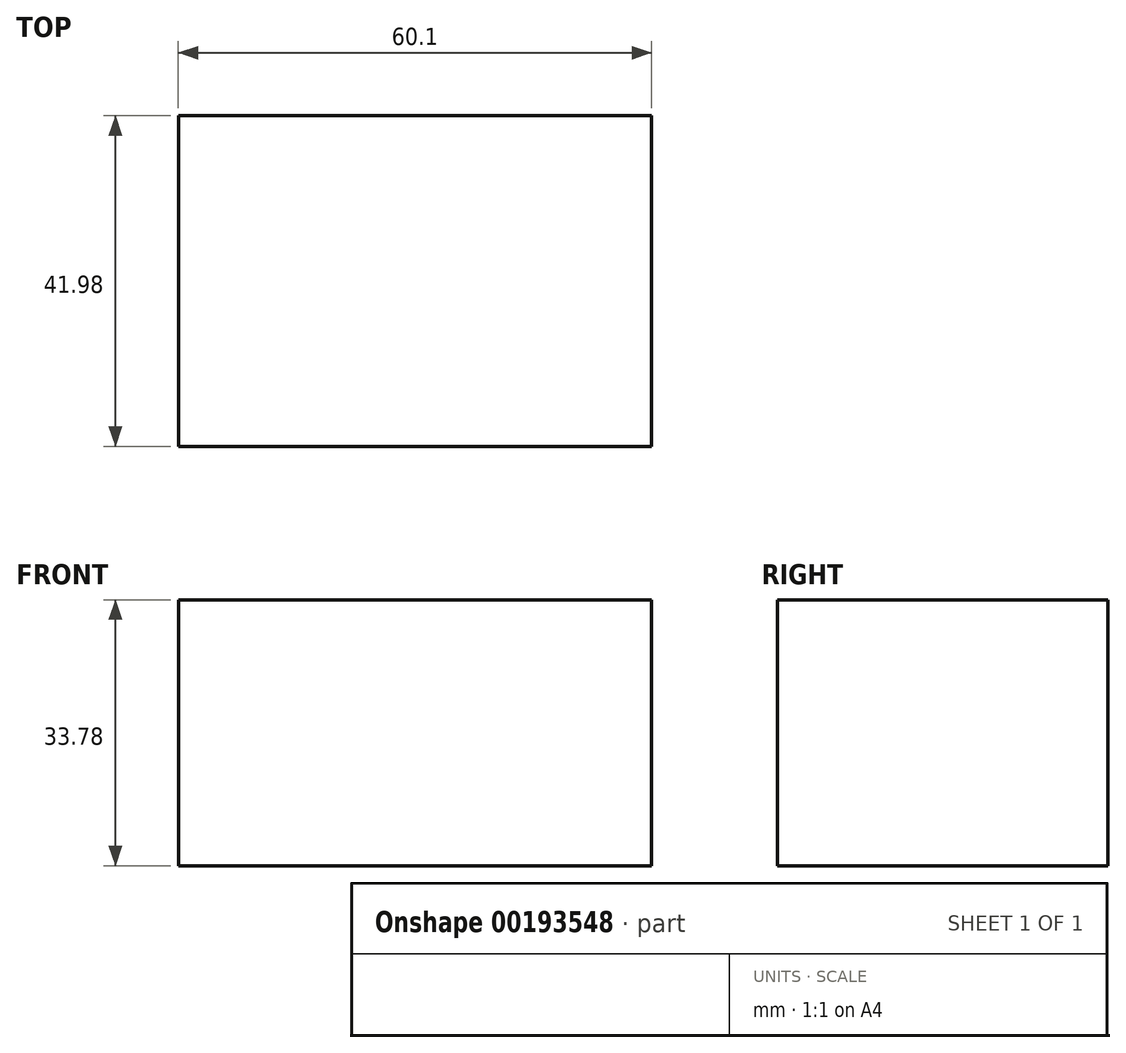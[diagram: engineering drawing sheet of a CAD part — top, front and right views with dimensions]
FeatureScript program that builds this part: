
annotation { "Feature Type Name" : "Feature", "Feature Type Description" : "" }
export const myFeature = defineFeature(function(context is Context, id is Id, definition is map)
    precondition{}
    {
        {
            var Q0;
            Q0=qCreatedBy(makeId("Top.planeOp"),FACE);
            var sketch = newSketch(context, id + "F0", { "sketchPlane" : qUnion([Q0])});
            skLineSegment(sketch, "E0.bottom", {"start": v(-30.05, -20.99) * mm, "end": v(30.05, -20.99) * mm});
            skLineSegment(sketch, "E0.top", {"start": v(-30.05, 20.99) * mm, "end": v(30.05, 20.99) * mm});
            skLineSegment(sketch, "E0.left", {"start": v(-30.05, -20.99) * mm, "end": v(-30.05, 20.99) * mm});
            skLineSegment(sketch, "E0.right", {"start": v(30.05, -20.99) * mm, "end": v(30.05, 20.99) * mm});
            skPoint(sketch, "E0.middle", {"position": v(0, 0) * mm});
            skSolve(sketch);
        }
        {
            var Q0;
            Q0 = qSketchRegion(id + "F0", true);
            extrude(context, id + "F1", {"entities" : qUnion([Q0]), "oppositeDirection" : true, "depth" : 33.78 * mm});
        }
    });
